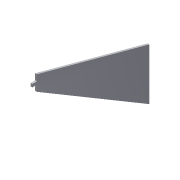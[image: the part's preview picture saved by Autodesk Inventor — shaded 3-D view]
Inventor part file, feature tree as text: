
AUTODESK INVENTOR PART (.ipt)
format: ipt  version: 2014 (Build 180170000, 170)  size: 81,408 bytes
history: native  units: mm
features: extrude x2, sketch x2
ambient origin geometry x8: Origin, YZ Plane, XZ Plane, XY Plane, X Axis, Y Axis, Z Axis, Center Point
bodies: Solid1 (feature_tree)
feature tree (4):
  extrude  "Extrusion1"  Depth=25.0mm
  extrude  "Extrusion2"  Depth=3.0mm TaperAngle=0.0deg
  sketch  "Sketch1"  dims[d0=25.0mm d1=85.0mm]
  sketch  "Sketch2"  dims[d2=185.0mm d3=3.0mm d4=0.0mm d5=5.0mm d6=7.5mm d7=10.0mm d8=3.0mm d9=0.0mm d10=25.0mm]
